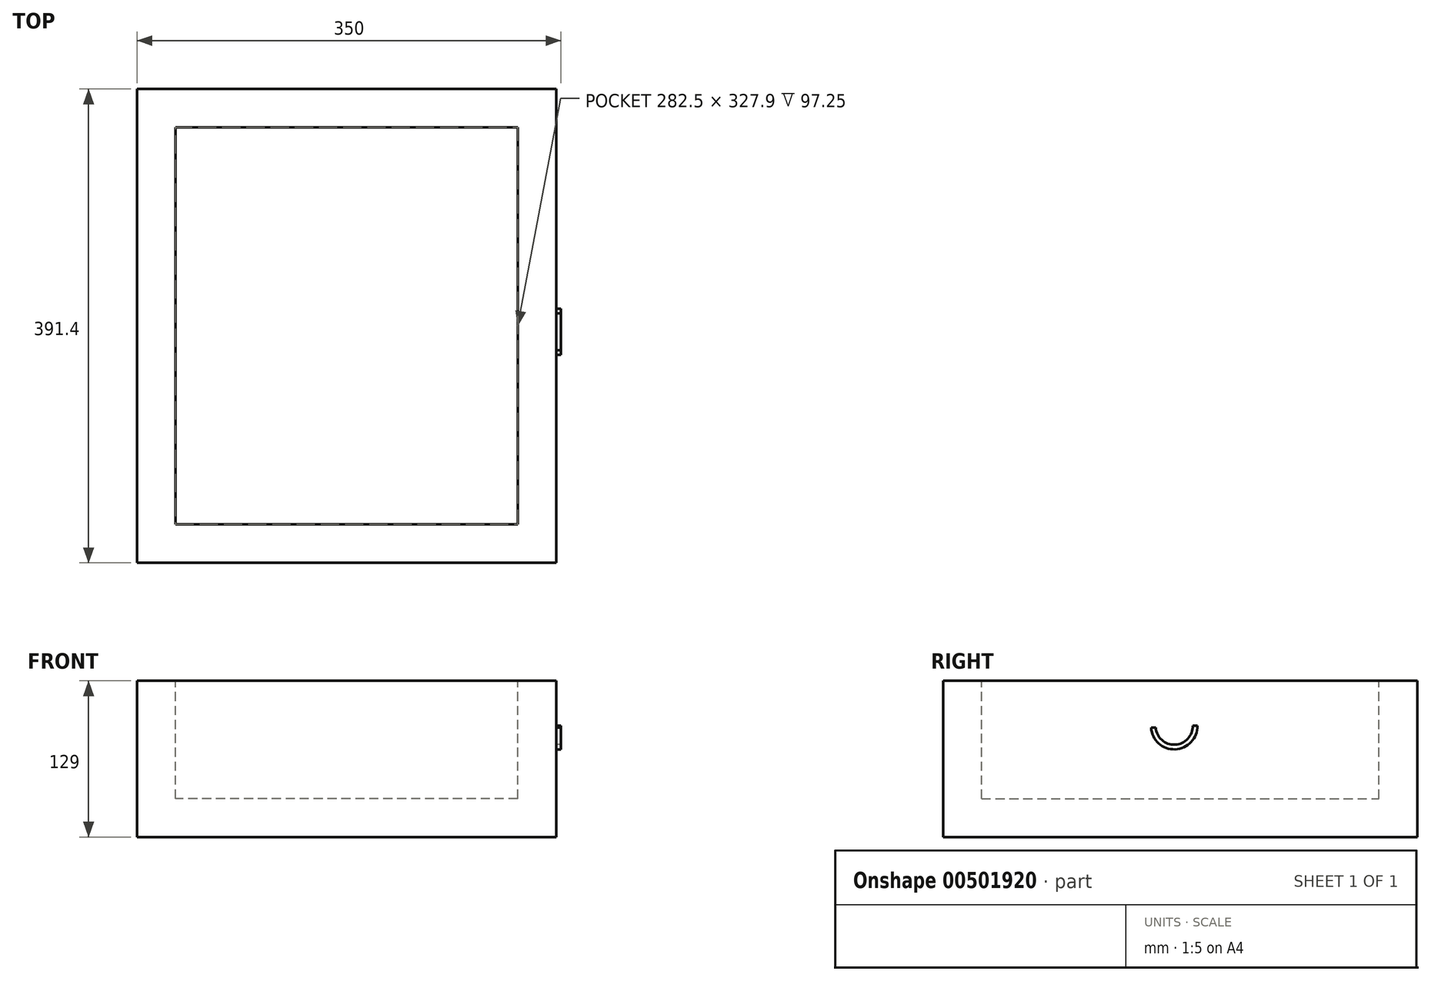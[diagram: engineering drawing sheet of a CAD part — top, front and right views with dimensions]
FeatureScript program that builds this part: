
annotation { "Feature Type Name" : "Feature", "Feature Type Description" : "" }
export const myFeature = defineFeature(function(context is Context, id is Id, definition is map)
    precondition{}
    {
        {
            var Q0;
            Q0=qCreatedBy(makeId("Front.planeOp"),FACE);
            var sketch = newSketch(context, id + "F0", { "sketchPlane" : qUnion([Q0])});
            skLineSegment(sketch, "E0.bottom", {"start": v(-173, 64.5) * mm, "end": v(173, 64.5) * mm});
            skLineSegment(sketch, "E0.top", {"start": v(-173, -64.5) * mm, "end": v(173, -64.5) * mm});
            skLineSegment(sketch, "E0.left", {"start": v(-173, 64.5) * mm, "end": v(-173, -64.5) * mm});
            skLineSegment(sketch, "E0.right", {"start": v(173, 64.5) * mm, "end": v(173, -64.5) * mm});
            skPoint(sketch, "E0.middle", {"position": v(0, 0) * mm});
            skSolve(sketch);
        }
        {
            var Q0;
            Q0 = qSketchRegion(id + "F0", true);
            var Q1;
            Q1 = qSketchRegion(id + "F2", true);
            extrude(context, id + "F1", {"entities" : qUnion([Q0, Q1]), "endBound" : BoundingType.SYMMETRIC, "depth" : 391.4 * mm});
        }
        {
            var Q0;
            Q0=makeQuery(id+"F1.opExtrude","SWEPT_FACE",FACE,{"disambiguationData":[OSD([sQuery(id+"F0.wireOp",EDGE,"E0.bottom")])]});
            var sketch = newSketch(context, id + "F2", { "sketchPlane" : qUnion([Q0])});
            skLineSegment(sketch, "E1.bottom", {"start": v(141.25, -163.95) * mm, "end": v(-141.25, -163.95) * mm});
            skLineSegment(sketch, "E1.top", {"start": v(141.25, 163.95) * mm, "end": v(-141.25, 163.95) * mm});
            skLineSegment(sketch, "E1.left", {"start": v(141.25, -163.95) * mm, "end": v(141.25, 163.95) * mm});
            skLineSegment(sketch, "E1.right", {"start": v(-141.25, -163.95) * mm, "end": v(-141.25, 163.95) * mm});
            skPoint(sketch, "E1.middle", {"position": v(0, 0) * mm});
            skSolve(sketch);
        }
        {
            var Q0;
            Q0 = qSketchRegion(id + "F2", true);
            extrude(context, id + "F3", {"entities" : qUnion([Q0]), "operationType" : NewBodyOperationType.REMOVE, "oppositeDirection" : true, "depth" : 129 * mm - 31.75 * mm});
        }
        {
            var Q0;
            Q0=makeQuery(id+"F1.opExtrude","SWEPT_FACE",FACE,{"disambiguationData":[OSD([sQuery(id+"F0.wireOp",EDGE,"E0.right")])]});
            var sketch = newSketch(context, id + "F4", { "sketchPlane" : qUnion([Q0])});
            skArc(sketch, "E2", {"start": v(-23.95, 25.92) * mm, "mid": v(-4.08, 7.91) * mm, "end": v(14.23, 27.5) * mm});
            skArc(sketch, "E3", {"start": v(-20.18, 25.92) * mm, "mid": v(-4.15, 11.77) * mm, "end": v(10.33, 27.5) * mm});
            skLineSegment(sketch, "E4", {"start": v(-20.18, 25.92) * mm, "end": v(-23.95, 25.92) * mm});
            skLineSegment(sketch, "E5", {"start": v(10.33, 27.5) * mm, "end": v(14.23, 27.5) * mm});
            skSolve(sketch);
        }
        {
            var Q0;
            Q0 = qSketchRegion(id + "F4", true);
            extrude(context, id + "F5", {"entities" : qUnion([Q0]), "operationType" : NewBodyOperationType.ADD, "depth" : 4 * mm});
        }
    });
